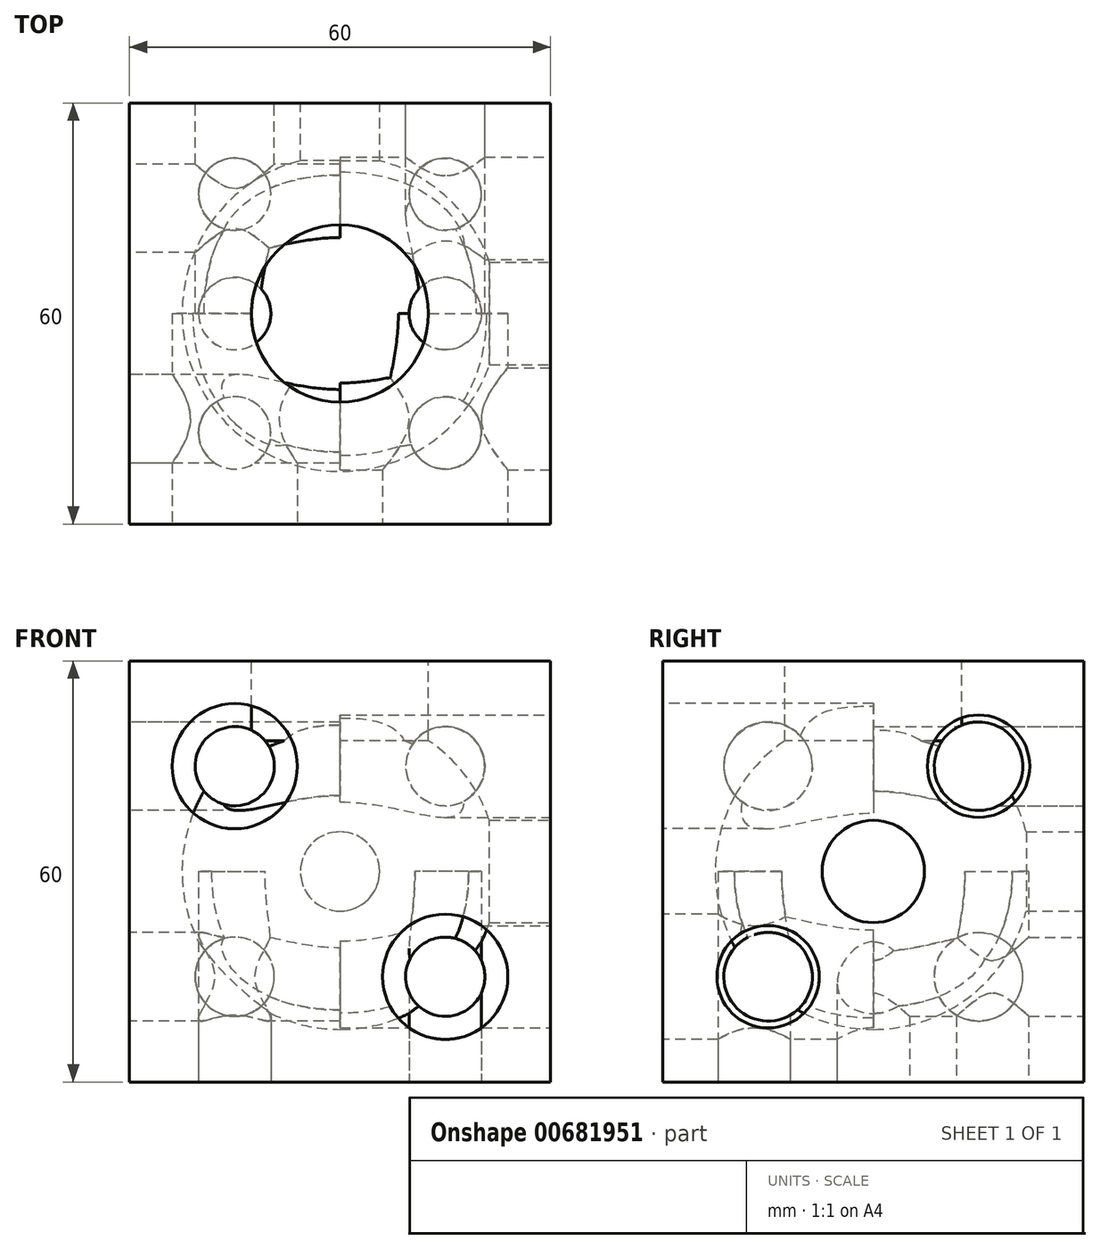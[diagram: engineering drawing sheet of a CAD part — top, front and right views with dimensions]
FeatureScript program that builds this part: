
annotation { "Feature Type Name" : "Feature", "Feature Type Description" : "" }
export const myFeature = defineFeature(function(context is Context, id is Id, definition is map)
    precondition{}
    {
        {
            var Q0;
            Q0=qCreatedBy(makeId("Top.planeOp"),FACE);
            var sketch = newSketch(context, id + "F0", { "sketchPlane" : qUnion([Q0])});
            skLineSegment(sketch, "E0.bottom", {"start": v(-30, 30) * mm, "end": v(30, 30) * mm});
            skLineSegment(sketch, "E0.top", {"start": v(-30, -30) * mm, "end": v(30, -30) * mm});
            skLineSegment(sketch, "E0.left", {"start": v(-30, 30) * mm, "end": v(-30, -30) * mm});
            skLineSegment(sketch, "E0.right", {"start": v(30, 30) * mm, "end": v(30, -30) * mm});
            skSolve(sketch);
        }
        {
            var Q0;
            Q0=makeQuery(id+"F0.imprint","IMPRINT",FACE,{"disambiguationData":[TD([[makeQuery(id+"F0.imprint","IMPRINT",EDGE,{"derivedFrom":sQuery(id+"F0.wireOp",EDGE,"E0.bottom")}),-1.0]])]});
            extrude(context, id + "F1", {"entities" : qUnion([Q0]), "depth" : 30 * mm, "offsetDistance" : 25 * mm, "hasSecondDirection" : true, "secondDirectionOppositeDirection" : true, "secondDirectionDepth" : 30 * mm});
        }
        {
            var Q0;
            Q0=makeQuery(id+"F1.opExtrude","CAP_FACE",FACE,{"disambiguationData":[OSD([sQuery(id+"F0.wireOp",EDGE,"E0.bottom"),sQuery(id+"F0.wireOp",EDGE,"E0.top"),sQuery(id+"F0.wireOp",EDGE,"E0.left"),sQuery(id+"F0.wireOp",EDGE,"E0.right")])],"isStart":false});
            var sketch = newSketch(context, id + "F2", { "sketchPlane" : qUnion([Q0])});
            skCircle(sketch, "E1", {"center": v(0, 0) * mm, "radius": 12.62 * mm});
            skSolve(sketch);
        }
        {
            var Q0;
            Q0=makeQuery(id+"F1.opExtrude","SWEPT_FACE",FACE,{"disambiguationData":[OSD([sQuery(id+"F0.wireOp",EDGE,"E0.top")])]});
            var sketch = newSketch(context, id + "F3", { "sketchPlane" : qUnion([Q0])});
            skLineSegment(sketch, "E2", {"start": v(-30, 30) * mm, "end": v(0, 0) * mm, "construction": true});
            skLineSegment(sketch, "E3", {"start": v(30, -30) * mm, "end": v(0, 0) * mm, "construction": true});
            skPoint(sketch, "E4", {"position": v(-15, 15) * mm});
            skPoint(sketch, "E5", {"position": v(15, -15) * mm});
            skCircle(sketch, "E6", {"center": v(-15, 15) * mm, "radius": 8.92 * mm});
            skCircle(sketch, "E7", {"center": v(15, -15) * mm, "radius": 8.92 * mm});
            skSolve(sketch);
        }
        {
            var Q0;
            Q0=makeQuery(id+"F1.opExtrude","SWEPT_FACE",FACE,{"disambiguationData":[OSD([sQuery(id+"F0.wireOp",EDGE,"E0.right")])]});
            var sketch = newSketch(context, id + "F4", { "sketchPlane" : qUnion([Q0])});
            skLineSegment(sketch, "E8", {"start": v(-30, -30) * mm, "end": v(0, 0) * mm, "construction": true});
            skLineSegment(sketch, "E9", {"start": v(0, 0) * mm, "end": v(30, 30) * mm, "construction": true});
            skPoint(sketch, "E10", {"position": v(-15, -15) * mm});
            skPoint(sketch, "E11", {"position": v(15, 15) * mm});
            skCircle(sketch, "E12", {"center": v(-15, -15) * mm, "radius": 7.29 * mm});
            skCircle(sketch, "E13", {"center": v(0, 0) * mm, "radius": 7.29 * mm});
            skCircle(sketch, "E14", {"center": v(15, 15) * mm, "radius": 7.29 * mm});
            skSolve(sketch);
        }
        {
            var Q0;
            Q0=makeQuery(id+"F1.opExtrude","SWEPT_FACE",FACE,{"disambiguationData":[OSD([sQuery(id+"F0.wireOp",EDGE,"E0.left")])]});
            var sketch = newSketch(context, id + "F5", { "sketchPlane" : qUnion([Q0])});
            skLineSegment(sketch, "E15", {"start": v(-30, 30) * mm, "end": v(0, 0) * mm, "construction": true});
            skLineSegment(sketch, "E16", {"start": v(0, 0) * mm, "end": v(30, 30) * mm, "construction": true});
            skLineSegment(sketch, "E17", {"start": v(30, 30) * mm, "end": v(30, -30) * mm, "construction": true});
            skLineSegment(sketch, "E18", {"start": v(30, -30) * mm, "end": v(0, 0) * mm, "construction": true});
            skLineSegment(sketch, "E19", {"start": v(-30, -30) * mm, "end": v(0, 0) * mm, "construction": true});
            skPoint(sketch, "E20", {"position": v(-15, 15) * mm});
            skPoint(sketch, "E21", {"position": v(-15, -15) * mm});
            skPoint(sketch, "E22", {"position": v(15, -15) * mm});
            skPoint(sketch, "E23", {"position": v(15, 15) * mm});
            skCircle(sketch, "E24", {"center": v(-15, 15) * mm, "radius": 6.3 * mm});
            skCircle(sketch, "E25", {"center": v(-15, -15) * mm, "radius": 6.3 * mm});
            skCircle(sketch, "E26", {"center": v(15, -15) * mm, "radius": 6.3 * mm});
            skCircle(sketch, "E27", {"center": v(15, 15) * mm, "radius": 6.3 * mm});
            skSolve(sketch);
        }
        {
            var Q0;
            Q0=makeQuery(id+"F1.opExtrude","SWEPT_FACE",FACE,{"disambiguationData":[OSD([sQuery(id+"F0.wireOp",EDGE,"E0.bottom")])]});
            var sketch = newSketch(context, id + "F6", { "sketchPlane" : qUnion([Q0])});
            skLineSegment(sketch, "E28", {"start": v(-30, 30) * mm, "end": v(0, 0) * mm, "construction": true});
            skLineSegment(sketch, "E29", {"start": v(0, 0) * mm, "end": v(30, -30) * mm, "construction": true});
            skLineSegment(sketch, "E30", {"start": v(30, -30) * mm, "end": v(30, 30) * mm, "construction": true});
            skLineSegment(sketch, "E31", {"start": v(30, 30) * mm, "end": v(0, 0) * mm, "construction": true});
            skLineSegment(sketch, "E32", {"start": v(0, 0) * mm, "end": v(-30, -30) * mm, "construction": true});
            skPoint(sketch, "E33", {"position": v(-15, 15) * mm});
            skPoint(sketch, "E34", {"position": v(-15, -15) * mm});
            skPoint(sketch, "E35", {"position": v(15, -15) * mm});
            skPoint(sketch, "E36", {"position": v(15, 15) * mm});
            skCircle(sketch, "E37", {"center": v(0, 0) * mm, "radius": 5.64 * mm});
            skCircle(sketch, "E38", {"center": v(-15, 15) * mm, "radius": 5.64 * mm});
            skCircle(sketch, "E39", {"center": v(-15, -15) * mm, "radius": 5.64 * mm});
            skCircle(sketch, "E40", {"center": v(15, -15) * mm, "radius": 5.64 * mm});
            skCircle(sketch, "E41", {"center": v(15, 15) * mm, "radius": 5.64 * mm});
            skSolve(sketch);
        }
        {
            var Q0;
            Q0=makeQuery(id+"F1.opExtrude","CAP_FACE",FACE,{"disambiguationData":[OSD([sQuery(id+"F0.wireOp",EDGE,"E0.bottom"),sQuery(id+"F0.wireOp",EDGE,"E0.top"),sQuery(id+"F0.wireOp",EDGE,"E0.left"),sQuery(id+"F0.wireOp",EDGE,"E0.right")])],"isStart":true});
            var sketch = newSketch(context, id + "F7", { "sketchPlane" : qUnion([Q0])});
            skLineSegment(sketch, "E42", {"start": v(30, -30) * mm, "end": v(30, 30) * mm, "construction": true});
            skLineSegment(sketch, "E43", {"start": v(-15, 30) * mm, "end": v(-15, 17) * mm, "construction": true});
            skLineSegment(sketch, "E44", {"start": v(-15, 17) * mm, "end": v(-15, 0) * mm, "construction": true});
            skLineSegment(sketch, "E45", {"start": v(-15, 0) * mm, "end": v(-15, -17) * mm, "construction": true});
            skLineSegment(sketch, "E46", {"start": v(-15, -17) * mm, "end": v(-15, -30) * mm, "construction": true});
            skLineSegment(sketch, "E47", {"start": v(-15, -30) * mm, "end": v(15, -30) * mm, "construction": true});
            skLineSegment(sketch, "E48", {"start": v(15, -30) * mm, "end": v(15, -17) * mm, "construction": true});
            skLineSegment(sketch, "E49", {"start": v(15, -17) * mm, "end": v(15, 0) * mm, "construction": true});
            skLineSegment(sketch, "E50", {"start": v(15, 0) * mm, "end": v(15, 17) * mm, "construction": true});
            skLineSegment(sketch, "E51", {"start": v(15, 17) * mm, "end": v(15, 30) * mm, "construction": true});
            skCircle(sketch, "E52", {"center": v(-15, 17) * mm, "radius": 5.15 * mm});
            skCircle(sketch, "E53", {"center": v(-15, 0) * mm, "radius": 5.15 * mm});
            skCircle(sketch, "E54", {"center": v(-15, -17) * mm, "radius": 5.15 * mm});
            skCircle(sketch, "E55", {"center": v(15, -17) * mm, "radius": 5.15 * mm});
            skCircle(sketch, "E56", {"center": v(15, 0) * mm, "radius": 5.15 * mm});
            skCircle(sketch, "E57", {"center": v(15, 17) * mm, "radius": 5.15 * mm});
            skSolve(sketch);
        }
        {
            var Q0;
            Q0=makeQuery(id+"F6.imprint","IMPRINT",FACE,{"disambiguationData":[TD([[makeQuery(id+"F6.imprint","IMPRINT",EDGE,{"derivedFrom":sQuery(id+"F6.wireOp",EDGE,"E41")}),1.0]])]});
            var Q1;
            Q1=makeQuery(id+"F6.imprint","IMPRINT",FACE,{"disambiguationData":[TD([[makeQuery(id+"F6.imprint","IMPRINT",EDGE,{"derivedFrom":sQuery(id+"F6.wireOp",EDGE,"E37")}),1.0]])]});
            var Q2;
            Q2=makeQuery(id+"F6.imprint","IMPRINT",FACE,{"disambiguationData":[TD([[makeQuery(id+"F6.imprint","IMPRINT",EDGE,{"derivedFrom":sQuery(id+"F6.wireOp",EDGE,"E38")}),1.0]])]});
            var Q3;
            Q3=makeQuery(id+"F6.imprint","IMPRINT",FACE,{"disambiguationData":[TD([[makeQuery(id+"F6.imprint","IMPRINT",EDGE,{"derivedFrom":sQuery(id+"F6.wireOp",EDGE,"E39")}),1.0]])]});
            var Q4;
            Q4=makeQuery(id+"F6.imprint","IMPRINT",FACE,{"disambiguationData":[TD([[makeQuery(id+"F6.imprint","IMPRINT",EDGE,{"derivedFrom":sQuery(id+"F6.wireOp",EDGE,"E40")}),1.0]])]});
            extrude(context, id + "F8", {"entities" : qUnion([Q0, Q1, Q2, Q3, Q4]), "operationType" : NewBodyOperationType.REMOVE, "oppositeDirection" : true, "depth" : 30 * mm, "offsetDistance" : 25 * mm});
        }
        {
            var Q0;
            Q0=makeQuery(id+"F2.imprint","IMPRINT",FACE,{"disambiguationData":[TD([[makeQuery(id+"F2.imprint","IMPRINT",EDGE,{"derivedFrom":sQuery(id+"F2.wireOp",EDGE,"E1")}),1.0]])]});
            extrude(context, id + "F9", {"entities" : qUnion([Q0]), "operationType" : NewBodyOperationType.REMOVE, "oppositeDirection" : true, "depth" : 30 * mm, "offsetDistance" : 25 * mm});
        }
        {
            var Q0;
            Q0=makeQuery(id+"F4.imprint","IMPRINT",FACE,{"disambiguationData":[TD([[makeQuery(id+"F4.imprint","IMPRINT",EDGE,{"derivedFrom":sQuery(id+"F4.wireOp",EDGE,"E14")}),1.0]])]});
            var Q1;
            Q1=makeQuery(id+"F4.imprint","IMPRINT",FACE,{"disambiguationData":[TD([[makeQuery(id+"F4.imprint","IMPRINT",EDGE,{"derivedFrom":sQuery(id+"F4.wireOp",EDGE,"E13")}),1.0]])]});
            var Q2;
            Q2=makeQuery(id+"F4.imprint","IMPRINT",FACE,{"disambiguationData":[TD([[makeQuery(id+"F4.imprint","IMPRINT",EDGE,{"derivedFrom":sQuery(id+"F4.wireOp",EDGE,"E12")}),1.0]])]});
            extrude(context, id + "F10", {"entities" : qUnion([Q0, Q1, Q2]), "operationType" : NewBodyOperationType.REMOVE, "oppositeDirection" : true, "depth" : 30 * mm, "offsetDistance" : 25 * mm});
        }
        {
            var Q0;
            Q0=makeQuery(id+"F3.imprint","IMPRINT",FACE,{"disambiguationData":[TD([[makeQuery(id+"F3.imprint","IMPRINT",EDGE,{"derivedFrom":sQuery(id+"F3.wireOp",EDGE,"E7")}),1.0]])]});
            var Q1;
            Q1=makeQuery(id+"F3.imprint","IMPRINT",FACE,{"disambiguationData":[TD([[makeQuery(id+"F3.imprint","IMPRINT",EDGE,{"derivedFrom":sQuery(id+"F3.wireOp",EDGE,"E6")}),1.0]])]});
            extrude(context, id + "F11", {"entities" : qUnion([Q0, Q1]), "operationType" : NewBodyOperationType.REMOVE, "oppositeDirection" : true, "depth" : 30 * mm, "offsetDistance" : 25 * mm});
        }
        {
            var Q0;
            Q0=makeQuery(id+"F7.imprint","IMPRINT",FACE,{"disambiguationData":[TD([[makeQuery(id+"F7.imprint","IMPRINT",EDGE,{"derivedFrom":sQuery(id+"F7.wireOp",EDGE,"E54")}),1.0]])]});
            var Q1;
            Q1=makeQuery(id+"F7.imprint","IMPRINT",FACE,{"disambiguationData":[TD([[makeQuery(id+"F7.imprint","IMPRINT",EDGE,{"derivedFrom":sQuery(id+"F7.wireOp",EDGE,"E53")}),1.0]])]});
            var Q2;
            Q2=makeQuery(id+"F7.imprint","IMPRINT",FACE,{"disambiguationData":[TD([[makeQuery(id+"F7.imprint","IMPRINT",EDGE,{"derivedFrom":sQuery(id+"F7.wireOp",EDGE,"E52")}),1.0]])]});
            var Q3;
            Q3=makeQuery(id+"F7.imprint","IMPRINT",FACE,{"disambiguationData":[TD([[makeQuery(id+"F7.imprint","IMPRINT",EDGE,{"derivedFrom":sQuery(id+"F7.wireOp",EDGE,"E57")}),1.0]])]});
            var Q4;
            Q4=makeQuery(id+"F7.imprint","IMPRINT",FACE,{"disambiguationData":[TD([[makeQuery(id+"F7.imprint","IMPRINT",EDGE,{"derivedFrom":sQuery(id+"F7.wireOp",EDGE,"E56")}),1.0]])]});
            var Q5;
            Q5=makeQuery(id+"F7.imprint","IMPRINT",FACE,{"disambiguationData":[TD([[makeQuery(id+"F7.imprint","IMPRINT",EDGE,{"derivedFrom":sQuery(id+"F7.wireOp",EDGE,"E55")}),1.0]])]});
            extrude(context, id + "F12", {"entities" : qUnion([Q0, Q1, Q2, Q3, Q4, Q5]), "operationType" : NewBodyOperationType.REMOVE, "oppositeDirection" : true, "depth" : 30 * mm, "offsetDistance" : 25 * mm});
        }
        {
            var Q0;
            Q0=makeQuery(id+"F5.imprint","IMPRINT",FACE,{"disambiguationData":[TD([[makeQuery(id+"F5.imprint","IMPRINT",EDGE,{"derivedFrom":sQuery(id+"F5.wireOp",EDGE,"E25")}),1.0]])]});
            var Q1;
            Q1=makeQuery(id+"F5.imprint","IMPRINT",FACE,{"disambiguationData":[TD([[makeQuery(id+"F5.imprint","IMPRINT",EDGE,{"derivedFrom":sQuery(id+"F5.wireOp",EDGE,"E24")}),1.0]])]});
            var Q2;
            Q2=makeQuery(id+"F5.imprint","IMPRINT",FACE,{"disambiguationData":[TD([[makeQuery(id+"F5.imprint","IMPRINT",EDGE,{"derivedFrom":sQuery(id+"F5.wireOp",EDGE,"E27")}),1.0]])]});
            var Q3;
            Q3=makeQuery(id+"F5.imprint","IMPRINT",FACE,{"disambiguationData":[TD([[makeQuery(id+"F5.imprint","IMPRINT",EDGE,{"derivedFrom":sQuery(id+"F5.wireOp",EDGE,"E26")}),1.0]])]});
            extrude(context, id + "F13", {"entities" : qUnion([Q0, Q1, Q2, Q3]), "operationType" : NewBodyOperationType.REMOVE, "oppositeDirection" : true, "depth" : 30 * mm, "offsetDistance" : 25 * mm});
        }
        {
            var Q0;
            Q0=qCreatedBy(makeId("Front.planeOp"),FACE);
            var sketch = newSketch(context, id + "F14", { "sketchPlane" : qUnion([Q0])});
            skCircle(sketch, "E58", {"center": v(0, 0) * mm, "radius": 22.5 * mm});
            skLineSegment(sketch, "E59", {"start": v(0, 22.5) * mm, "end": v(0, -22.5) * mm});
            skSolve(sketch);
        }
        {
            var Q0;
            {var subQ0=sQuery(id+"F14.wireOp",EDGE,"E59");Q0=makeQuery(id+"F14.imprint","IMPRINT",FACE,{"disambiguationData":[TD([[makeQuery(id+"F14.imprint","IMPRINT",EDGE,{"derivedFrom":subQ0}),1.0]])]});}
            var Q1;
            Q1=sQuery(id+"F14.wireOp",EDGE,"E59");
            revolve(context, id + "F15", {"operationType" : NewBodyOperationType.REMOVE, "entities" : qUnion([Q0]), "axis" : qUnion([Q1]), "revolveType" : RevolveType.FULL, "oppositeDirection" : true});
        }
    });
